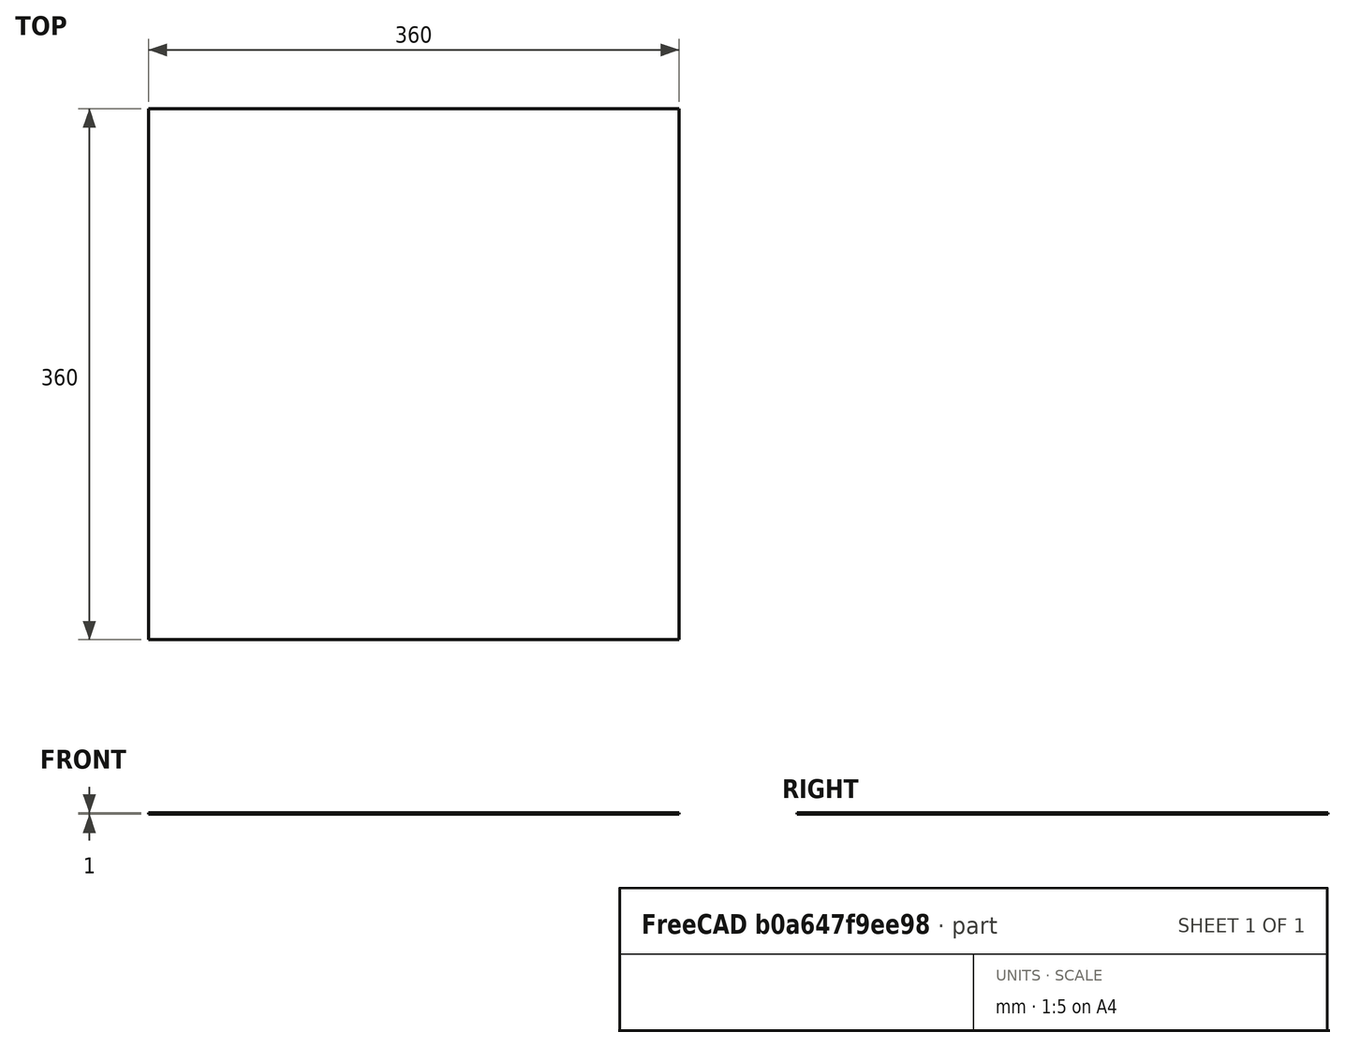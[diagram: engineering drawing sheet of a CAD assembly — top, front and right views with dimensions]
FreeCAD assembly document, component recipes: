
FREECAD ASSEMBLY — COMPONENT RECIPES ("parabolic_simulation")

This assembly document has 3 components, labeled P0..P2 below (a component is one placed body or linked part). 3 of them carry a construction recipe — the FreeCAD feature program that regenerates the part from scratch, quoted from this document or its linked companion documents; the rest are supplied as boundary geometry only. No exploded tour is included for this assembly.
COMPONENT P0 — recipe-attached ("TemOctagon", a linked part whose construction recipe lives in a companion FreeCAD document of the same project; that document's serialized recipe follows).
Construction recipe (the companion document, serialized — sketch geometry with constraints, then the solid features built on it; lengths are millimeters unless a unit is written):

FCSTD DOCUMENT  (FreeCAD 0.20R29603 (Git))
Label: tem_octagon
License: All rights reserved
LicenseURL: http://en.wikipedia.org/wiki/All_rights_reserved
objects: Part::Compound×18, Part::Cylinder×16, Part::Cut×10, Part::Feature×8, Part::FeaturePython×8, Part::Part2DObjectPython×2, Part::Extrusion×2
note: 64 computed .brp shape members not serialized (recipe doc carries the construction recipe); baked Part::Feature solids carry a one-line shape summary decoded from their .brp

FEATURE [Part::Part2DObjectPython] Wire  # Draft 2D object (typed FeaturePython)
  Area = 106458
  ChamferSize = 0
  Closed = true
  End = (74.24,179.24,-40)
  FilletRadius = 0
  Length = 1187.89
  MakeFace = true
  Placement = pos=(0,0,-40) rot=(0,0,1;0rad)
  Points = (9) [(74.24,179.24,-2.13163e-14),(179.24,74.24,0),(179.24,-74.24,0),(74.24,-179.24,0),(-74.24,-179.24,0),(-179.24,-74.24,0),(-179.24,74.24,0),(-74.24,179.24,0),(74.24,179.24,-2.13163e-14)]
  Start = (74.24,179.24,-40)
  Subdivisions = 0
FEATURE [Part::Extrusion] Extrude
  Base = -> Wire
  Dir = (0,0,1)
  DirMode = 2
  FaceMakerClass = Part::FaceMakerBullseye
  LengthFwd = 80
  LengthRev = 0
  Solid = false
  Symmetric = false
FEATURE [Part::Part2DObjectPython] Wire001  # Draft 2D object (typed FeaturePython)
  Area = 85639.1
  ChamferSize = 0
  Closed = true
  End = (66.59,160.76,-40)
  FilletRadius = 0
  Length = 1065.43
  MakeFace = true
  Placement = pos=(0,0,-40) rot=(0,0,1;0rad)
  Points = (9) [(66.59,160.76,0),(160.76,66.59,0),(160.76,-66.59,0),(66.59,-160.76,0),(-66.59,-160.76,0),(-160.76,-66.59,0),(-160.76,66.59,0),(-66.59,160.76,0),(66.59,160.76,0)]
  Start = (66.59,160.76,-40)
  Subdivisions = 0
FEATURE [Part::Extrusion] Extrude001
  Base = -> Wire001
  Dir = (0,0,1)
  DirMode = 2
  FaceMakerClass = Part::FaceMakerBullseye
  LengthFwd = 80
  LengthRev = 0
  Solid = false
  Symmetric = false
FEATURE [Part::Cut] Cut
  Base = -> Extrude
  Tool = -> Extrude001
FEATURE [Part::Feature] Solid  label="Hositrad_CF35-Blank"
  Placement = pos=(0,166.75,0) rot=(0,0,1;0rad)
  shape: bbox 70 x 12.7 x 70 mm, 58 faces (baked)
FEATURE [Part::Cylinder] Cylinder  label="Zylinder"
  Angle = 360
  AttacherType = Attacher::AttachEngine3D
  FirstAngle = 0
  Height = 20
  Placement = pos=(0,179.75,0) rot=(1,0,0;1.5708rad)
  Radius = 34.5
  SecondAngle = 0
FEATURE [Part::Cylinder] Cylinder001  label="Zylinder001"
  Angle = 360
  AttacherType = Attacher::AttachEngine3D
  FirstAngle = 0
  Height = 20
  Placement = pos=(0,179.75,0) rot=(1,0,0;1.5708rad)
  Radius = 22.25
  SecondAngle = 0
FEATURE [Part::Cylinder] Cylinder002  label="Zylinder002"
  Angle = 360
  AttacherType = Attacher::AttachEngine3D
  FirstAngle = 0
  Height = 20
  Placement = pos=(0,179.75,0) rot=(1,0,0;1.5708rad)
  Radius = 34.5
  SecondAngle = 0
FEATURE [Part::Compound] Compound
  Links = -> [Cylinder002]
  Placement = pos=(0,0,0) rot=(0,0,1;0.785398rad)
FEATURE [Part::Cylinder] Cylinder003  label="Zylinder003"
  Angle = 360
  AttacherType = Attacher::AttachEngine3D
  FirstAngle = 0
  Height = 20
  Placement = pos=(0,179.75,0) rot=(1,0,0;1.5708rad)
  Radius = 34.5
  SecondAngle = 0
FEATURE [Part::Compound] Compound001
  Links = -> [Cylinder003]
  Placement = pos=(0,0,0) rot=(0,0,1;1.5708rad)
FEATURE [Part::Cylinder] Cylinder004  label="Zylinder004"
  Angle = 360
  AttacherType = Attacher::AttachEngine3D
  FirstAngle = 0
  Height = 20
  Placement = pos=(0,179.75,0) rot=(1,0,0;1.5708rad)
  Radius = 34.5
  SecondAngle = 0
FEATURE [Part::Compound] Compound002
  Links = -> [Cylinder004]
  Placement = pos=(0,0,0) rot=(0,0,1;2.35619rad)
FEATURE [Part::Cylinder] Cylinder005  label="Zylinder005"
  Angle = 360
  AttacherType = Attacher::AttachEngine3D
  FirstAngle = 0
  Height = 20
  Placement = pos=(0,179.75,0) rot=(1,0,0;1.5708rad)
  Radius = 34.5
  SecondAngle = 0
FEATURE [Part::Compound] Compound003
  Links = -> [Cylinder005]
  Placement = pos=(0,0,0) rot=(0,0,1;3.14159rad)
FEATURE [Part::Cylinder] Cylinder006  label="Zylinder006"
  Angle = 360
  AttacherType = Attacher::AttachEngine3D
  FirstAngle = 0
  Height = 20
  Placement = pos=(0,179.75,0) rot=(1,0,0;1.5708rad)
  Radius = 34.5
  SecondAngle = 0
FEATURE [Part::Compound] Compound004
  Links = -> [Cylinder006]
  Placement = pos=(0,0,0) rot=(0,0,1;3.92699rad)
FEATURE [Part::Cylinder] Cylinder007  label="Zylinder007"
  Angle = 360
  AttacherType = Attacher::AttachEngine3D
  FirstAngle = 0
  Height = 20
  Placement = pos=(0,179.75,0) rot=(1,0,0;1.5708rad)
  Radius = 34.5
  SecondAngle = 0
FEATURE [Part::Compound] Compound005
  Links = -> [Cylinder007]
  Placement = pos=(0,0,0) rot=(0,0,1;4.71239rad)
FEATURE [Part::Cylinder] Cylinder008  label="Zylinder008"
  Angle = 360
  AttacherType = Attacher::AttachEngine3D
  FirstAngle = 0
  Height = 20
  Placement = pos=(0,179.75,0) rot=(1,0,0;1.5708rad)
  Radius = 34.5
  SecondAngle = 0
FEATURE [Part::Compound] Compound006
  Links = -> [Cylinder008]
  Placement = pos=(0,0,0) rot=(0,0,1;5.49779rad)
FEATURE [Part::Compound] Compound007
  Links = -> [Cylinder,Compound,Compound001,Compound002,Compound003,Compound004,Compound005,Compound006]
FEATURE [Part::Cut] Cut001
  Base = -> Cut
  Tool = -> Compound007
FEATURE [Part::Cut] Cut002
  Base = -> Solid
  Tool = -> Cylinder001
FEATURE [Part::FeaturePython] Tube  # WARN: FeaturePython — macro-defined, semantics opaque (R4)
  AttacherType = Attacher::AttachEngine3D
  Height = 6
  InnerRadius = 22.25
  OuterRadius = 34.5
  Placement = pos=(0,166.76,0) rot=(1,0,0;1.5708rad)
FEATURE [Part::Compound] Compound008
  Links = -> [Tube,Cut002]
FEATURE [Part::Cylinder] Cylinder009  label="Zylinder009"
  Angle = 360
  AttacherType = Attacher::AttachEngine3D
  FirstAngle = 0
  Height = 20
  Placement = pos=(0,179.75,0) rot=(1,0,0;1.5708rad)
  Radius = 22.25
  SecondAngle = 0
FEATURE [Part::Feature] Solid001  label="Hositrad_CF35-Blank001"
  Placement = pos=(0,166.75,0) rot=(0,0,1;0rad)
  shape: bbox 70 x 12.7 x 70 mm, 58 faces (baked)
FEATURE [Part::Cut] Cut003
  Base = -> Solid001
  Tool = -> Cylinder009
FEATURE [Part::FeaturePython] Tube001  # WARN: FeaturePython — macro-defined, semantics opaque (R4)
  AttacherType = Attacher::AttachEngine3D
  Height = 6
  InnerRadius = 22.25
  OuterRadius = 34.5
  Placement = pos=(0,166.76,0) rot=(1,0,0;1.5708rad)
FEATURE [Part::Compound] Compound009
  Links = -> [Tube001,Cut003]
  Placement = pos=(0,0,0) rot=(0,0,1;0.785398rad)
FEATURE [Part::Cylinder] Cylinder010  label="Zylinder010"
  Angle = 360
  AttacherType = Attacher::AttachEngine3D
  FirstAngle = 0
  Height = 20
  Placement = pos=(0,179.75,0) rot=(1,0,0;1.5708rad)
  Radius = 22.25
  SecondAngle = 0
FEATURE [Part::Feature] Solid002  label="Hositrad_CF35-Blank002"
  Placement = pos=(0,166.75,0) rot=(0,0,1;0rad)
  shape: bbox 70 x 12.7 x 70 mm, 58 faces (baked)
FEATURE [Part::Cut] Cut004
  Base = -> Solid002
  Tool = -> Cylinder010
FEATURE [Part::FeaturePython] Tube002  # WARN: FeaturePython — macro-defined, semantics opaque (R4)
  AttacherType = Attacher::AttachEngine3D
  Height = 6
  InnerRadius = 22.25
  OuterRadius = 34.5
  Placement = pos=(0,166.76,0) rot=(1,0,0;1.5708rad)
FEATURE [Part::Compound] Compound010
  Links = -> [Tube002,Cut004]
  Placement = pos=(0,0,0) rot=(0,0,1;1.5708rad)
FEATURE [Part::Cylinder] Cylinder011  label="Zylinder011"
  Angle = 360
  AttacherType = Attacher::AttachEngine3D
  FirstAngle = 0
  Height = 20
  Placement = pos=(0,179.75,0) rot=(1,0,0;1.5708rad)
  Radius = 22.25
  SecondAngle = 0
FEATURE [Part::Feature] Solid003  label="Hositrad_CF35-Blank003"
  Placement = pos=(0,166.75,0) rot=(0,0,1;0rad)
  shape: bbox 70 x 12.7 x 70 mm, 58 faces (baked)
FEATURE [Part::Cut] Cut005
  Base = -> Solid003
  Tool = -> Cylinder011
FEATURE [Part::FeaturePython] Tube003  # WARN: FeaturePython — macro-defined, semantics opaque (R4)
  AttacherType = Attacher::AttachEngine3D
  Height = 6
  InnerRadius = 22.25
  OuterRadius = 34.5
  Placement = pos=(0,166.76,0) rot=(1,0,0;1.5708rad)
FEATURE [Part::Compound] Compound011
  Links = -> [Tube003,Cut005]
  Placement = pos=(0,0,0) rot=(0,0,1;2.35619rad)
FEATURE [Part::Cylinder] Cylinder012  label="Zylinder012"
  Angle = 360
  AttacherType = Attacher::AttachEngine3D
  FirstAngle = 0
  Height = 20
  Placement = pos=(0,179.75,0) rot=(1,0,0;1.5708rad)
  Radius = 22.25
  SecondAngle = 0
FEATURE [Part::Feature] Solid004  label="Hositrad_CF35-Blank004"
  Placement = pos=(0,166.75,0) rot=(0,0,1;0rad)
  shape: bbox 70 x 12.7 x 70 mm, 58 faces (baked)
FEATURE [Part::Cut] Cut006
  Base = -> Solid004
  Tool = -> Cylinder012
FEATURE [Part::FeaturePython] Tube004  # WARN: FeaturePython — macro-defined, semantics opaque (R4)
  AttacherType = Attacher::AttachEngine3D
  Height = 6
  InnerRadius = 22.25
  OuterRadius = 34.5
  Placement = pos=(0,166.76,0) rot=(1,0,0;1.5708rad)
FEATURE [Part::Compound] Compound012
  Links = -> [Tube004,Cut006]
  Placement = pos=(0,0,0) rot=(0,0,1;3.14159rad)
FEATURE [Part::Cylinder] Cylinder013  label="Zylinder013"
  Angle = 360
  AttacherType = Attacher::AttachEngine3D
  FirstAngle = 0
  Height = 20
  Placement = pos=(0,179.75,0) rot=(1,0,0;1.5708rad)
  Radius = 22.25
  SecondAngle = 0
FEATURE [Part::Feature] Solid005  label="Hositrad_CF35-Blank005"
  Placement = pos=(0,166.75,0) rot=(0,0,1;0rad)
  shape: bbox 70 x 12.7 x 70 mm, 58 faces (baked)
FEATURE [Part::Cut] Cut007
  Base = -> Solid005
  Tool = -> Cylinder013
FEATURE [Part::FeaturePython] Tube005  # WARN: FeaturePython — macro-defined, semantics opaque (R4)
  AttacherType = Attacher::AttachEngine3D
  Height = 6
  InnerRadius = 22.25
  OuterRadius = 34.5
  Placement = pos=(0,166.76,0) rot=(1,0,0;1.5708rad)
FEATURE [Part::Compound] Compound013
  Links = -> [Tube005,Cut007]
  Placement = pos=(0,0,0) rot=(0,0,1;3.92699rad)
FEATURE [Part::Cylinder] Cylinder014  label="Zylinder014"
  Angle = 360
  AttacherType = Attacher::AttachEngine3D
  FirstAngle = 0
  Height = 20
  Placement = pos=(0,179.75,0) rot=(1,0,0;1.5708rad)
  Radius = 22.25
  SecondAngle = 0
FEATURE [Part::Feature] Solid006  label="Hositrad_CF35-Blank006"
  Placement = pos=(0,166.75,0) rot=(0,0,1;0rad)
  shape: bbox 70 x 12.7 x 70 mm, 58 faces (baked)
FEATURE [Part::Cut] Cut008
  Base = -> Solid006
  Tool = -> Cylinder014
FEATURE [Part::FeaturePython] Tube006  # WARN: FeaturePython — macro-defined, semantics opaque (R4)
  AttacherType = Attacher::AttachEngine3D
  Height = 6
  InnerRadius = 22.25
  OuterRadius = 34.5
  Placement = pos=(0,166.76,0) rot=(1,0,0;1.5708rad)
FEATURE [Part::Compound] Compound014
  Links = -> [Tube006,Cut008]
  Placement = pos=(0,0,0) rot=(0,0,1;4.71239rad)
FEATURE [Part::Cylinder] Cylinder015  label="Zylinder015"
  Angle = 360
  AttacherType = Attacher::AttachEngine3D
  FirstAngle = 0
  Height = 20
  Placement = pos=(0,179.75,0) rot=(1,0,0;1.5708rad)
  Radius = 22.25
  SecondAngle = 0
FEATURE [Part::Feature] Solid007  label="Hositrad_CF35-Blank007"
  Placement = pos=(0,166.75,0) rot=(0,0,1;0rad)
  shape: bbox 70 x 12.7 x 70 mm, 58 faces (baked)
FEATURE [Part::Cut] Cut009
  Base = -> Solid007
  Tool = -> Cylinder015
FEATURE [Part::FeaturePython] Tube007  # WARN: FeaturePython — macro-defined, semantics opaque (R4)
  AttacherType = Attacher::AttachEngine3D
  Height = 6
  InnerRadius = 22.25
  OuterRadius = 34.5
  Placement = pos=(0,166.76,0) rot=(1,0,0;1.5708rad)
FEATURE [Part::Compound] Compound015
  Links = -> [Tube007,Cut009]
  Placement = pos=(0,0,0) rot=(0,0,1;5.49779rad)
FEATURE [Part::Compound] Compound016
  Links = -> [Compound008,Compound009,Compound010,Compound011,Compound012,Compound013,Compound014,Compound015]
FEATURE [Part::Compound] Compound017
  Links = -> [Cut001,Compound016]
COMPONENT P1 — recipe-attached ("ParabolicMirrorWithScrewmount", a linked part whose construction recipe lives in a companion FreeCAD document of the same project; that document's serialized recipe follows).
Construction recipe (the companion document, serialized — sketch geometry with constraints, then the solid features built on it; lengths are millimeters unless a unit is written):

FCSTD DOCUMENT  (FreeCAD 0.19R24267 +99 (Git))
Label: parabolic_screwmount
License: All rights reserved
LicenseURL: http://en.wikipedia.org/wiki/All_rights_reserved
objects: Part::Cylinder×4, Part::Box×2, App::Link×1, Spreadsheet::Sheet×1, Part::Compound×1, Part::MultiFuse×1, Part::Cut×1
note: 9 computed .brp shape members not serialized (recipe doc carries the construction recipe); baked Part::Feature solids carry a one-line shape summary decoded from their .brp
EXTERNAL_REF file=parabolic_base.FCStd obj=Common
EXTERNAL_REF file=parabolic_base.FCStd obj=Spreadsheet

FEATURE [App::Link] Link  label="MirrorWithoutMount_Solid"
  LinkedObject = -> <external parabolic_base.FCStd>#Common
FEATURE [Spreadsheet::Sheet] Spreadsheet  label="ScrewMountParameters"
  cells = A1=Settings; E1=Importet properties (don't change here!); A2=Screw type; B2=M1; C2=Informative only (not updating below values); E2=Body offset; F2(body_offset)==<<parabolic_base>>#<<MirrorParameters>>.center_offset + <<parabolic_base>>#<<MirrorParameters>>.focal_length; G2=From parabolic_base: Offset of the body part with relation to Origin at the beamhole; A3=Through hole diameter; B3(mountscrew_through_dia)=1.2; C3=Close or medium fit diameter; E3=Body length; F3(body_length)==<<parabolic_base>>#<<MirrorParameters>>.tot_length; G3=From parabolic_base: Length of the body part; A4=Minimum material thickness; B4(min_material_thickness)=0.5; C4=Leave at least this amount of material if possible; E4=Body diameter; F4(body_width)==<<parabolic_base>>#<<MirrorParameters>>.max_width; G4=From parabolic_base: Diameter of body (max. width); A5=Screw head diameter; B5(screwhead_dia)=2; C5=Diameter of screw head; E5=Body height; F5(body_height)==<<parabolic_base>>#<<MirrorParameters>>.max_height; G5=From parabolic_base: Height of body (max body); A6=Screw head height max; B6(screwhead_height_max)==sqrt((body_width / 2) ^ 2 - (screwhead_dia / 2) ^ 2) - min_material_thickness; C6=Absolute maximum that leaves minimum material intact; A7=Screw head height real; B7(screwhead_height)=0.7; C7=Height of screw head; A8=Remaining material below screw head; B8(calculated_remaining_below_screwhead)==sqrt((body_width / 2) ^ 2 - (screwhead_dia / 2) ^ 2) - screwhead_height; C8=Remaining material below head of screw; A9=Remaining material on side of screw head; B9==(body_width - screwhead_dia) / 2; C9=Remaining material on both sides of the screw head; A10=Remaining material on side of screw; B10==(body_width - mountscrew_through_dia) / 2; C10=Remaining material on both sides of the screw
FEATURE [Part::Box] Box  label="CuttingToolThroughHole"
  AttacherType = Attacher::AttachEngine3D
  Height = 1.7
  Length = 4
  Placement = pos=(2.25,-0.6,0) rot=(0,0,1;0rad)
  Width = 1.2
  expr: Width = <<ScrewMountParameters>>.mountscrew_through_dia
  expr: Length = <<ScrewMountParameters>>.body_length - 2 * <<ScrewMountParameters>>.min_material_thickness - <<ScrewMountParameters>>.screwhead_dia
  expr: Height = <<ScrewMountParameters>>.body_height
  expr: .Placement.Base.y = -<<ScrewMountParameters>>.mountscrew_through_dia / 2
  expr: .Placement.Base.x = <<ScrewMountParameters>>.body_offset + <<ScrewMountParameters>>.min_material_thickness + <<ScrewMountParameters>>.screwhead_dia / 2
FEATURE [Part::Box] Box001  label="CuttingToolScrewHead"
  AttacherType = Attacher::AttachEngine3D
  Height = 0.942264
  Length = 4
  Placement = pos=(2.25,-1,1.24274) rot=(0,0,1;0rad)
  Width = 2
  expr: Width = <<ScrewMountParameters>>.screwhead_dia
  expr: Length = <<ScrewMountParameters>>.body_length - 2 * <<ScrewMountParameters>>.min_material_thickness - <<ScrewMountParameters>>.screwhead_dia
  expr: Height = <<ScrewMountParameters>>.body_width / 2 - <<ScrewMountParameters>>.calculated_remaining_below_screwhead
  expr: .Placement.Base.z = <<ScrewMountParameters>>.calculated_remaining_below_screwhead
  expr: .Placement.Base.y = -<<ScrewMountParameters>>.screwhead_dia / 2
  expr: .Placement.Base.x = <<ScrewMountParameters>>.body_offset + <<ScrewMountParameters>>.min_material_thickness + <<ScrewMountParameters>>.screwhead_dia / 2
FEATURE [Part::Compound] Compound
  Links = -> [Link]
FEATURE [Part::Cylinder] Cylinder  label="HeadFront"
  Angle = 360
  AttacherType = Attacher::AttachEngine3D
  Height = 10
  Placement = pos=(2.25,0,1.24274) rot=(0,0,1;0rad)
  Radius = 1
  expr: .Placement.Base.x = <<ScrewMountParameters>>.body_offset + <<ScrewMountParameters>>.min_material_thickness + <<ScrewMountParameters>>.screwhead_dia / 2
  expr: .Placement.Base.z = <<ScrewMountParameters>>.calculated_remaining_below_screwhead
  expr: Radius = <<ScrewMountParameters>>.screwhead_dia / 2
FEATURE [Part::Cylinder] Cylinder001  label="HeadBack"
  Angle = 360
  AttacherType = Attacher::AttachEngine3D
  Height = 10
  Placement = pos=(6.25,0,1.24274) rot=(0,0,1;0rad)
  Radius = 1
  expr: Radius = <<ScrewMountParameters>>.screwhead_dia / 2
  expr: .Placement.Base.z = <<ScrewMountParameters>>.calculated_remaining_below_screwhead
  expr: .Placement.Base.x = <<ScrewMountParameters>>.body_offset + <<ScrewMountParameters>>.min_material_thickness + <<ScrewMountParameters>>.screwhead_dia / 2 + <<ScrewMountParameters>>.body_length - 2 * <<ScrewMountParameters>>.min_material_thickness - <<ScrewMountParameters>>.screwhead_dia
FEATURE [Part::Cylinder] Cylinder002  label="ScrewThroughFront"
  Angle = 360
  AttacherType = Attacher::AttachEngine3D
  Height = 10
  Placement = pos=(2.25,0,0) rot=(0,0,1;0rad)
  Radius = 0.6
  expr: .Placement.Base.y = 0
  expr: Radius = <<ScrewMountParameters>>.mountscrew_through_dia / 2
  expr: .Placement.Base.x = <<ScrewMountParameters>>.body_offset + <<ScrewMountParameters>>.min_material_thickness + <<ScrewMountParameters>>.screwhead_dia / 2
FEATURE [Part::Cylinder] Cylinder003  label="ScrewThroughBack"
  Angle = 360
  AttacherType = Attacher::AttachEngine3D
  Height = 10
  Placement = pos=(6.25,0,0) rot=(0,0,1;0rad)
  Radius = 0.6
  expr: .Placement.Base.x = <<ScrewMountParameters>>.body_offset + <<ScrewMountParameters>>.min_material_thickness + <<ScrewMountParameters>>.screwhead_dia / 2 + <<ScrewMountParameters>>.body_length - 2 * <<ScrewMountParameters>>.min_material_thickness - <<ScrewMountParameters>>.screwhead_dia
  expr: Radius = <<ScrewMountParameters>>.mountscrew_through_dia / 2
FEATURE [Part::MultiFuse] Fusion  label="CuttingTools"
  Shapes = -> [Box001,Box,Cylinder,Cylinder001,Cylinder002,Cylinder003]
FEATURE [Part::Cut] Cut  label="ParabolicMirrorWithScrewmount"
  Base = -> Compound
  Tool = -> Fusion
COMPONENT P2 — recipe-attached ("TemHolder", a linked part whose construction recipe lives in a companion FreeCAD document of the same project; that document's serialized recipe follows).
Construction recipe (the companion document, serialized — sketch geometry with constraints, then the solid features built on it; lengths are millimeters unless a unit is written):

FCSTD DOCUMENT  (FreeCAD 0.21R33675 (Git))
Label: temholder2
License: All rights reserved
LicenseURL: http://en.wikipedia.org/wiki/All_rights_reserved
objects: TechDraw::DrawViewDimension×22, Part::Cylinder×10, TechDraw::DrawProjGroupItem×10, Part::Cut×8, Part::Box×7, Part::MultiFuse×6, TechDraw::DrawSVGTemplate×2, TechDraw::DrawProjGroup×2, TechDraw::DrawPage×2, Part::MultiCommon×1
note: 32 computed .brp shape members not serialized (recipe doc carries the construction recipe); baked Part::Feature solids carry a one-line shape summary decoded from their .brp

FEATURE [Part::Cylinder] Cylinder  label="Zylinder"
  Angle = 360
  AttacherType = Attacher::AttachEngine3D
  FirstAngle = 0
  Height = 21.5
  Placement = pos=(0,0,-0.5) rot=(0,0,1;0rad)
  Radius = 2.2
  SecondAngle = 0
FEATURE [Part::Cylinder] Cylinder001  label="Zylinder001"
  Angle = 360
  AttacherType = Attacher::AttachEngine3D
  FirstAngle = 0
  Height = 18
  Placement = pos=(0,0,5) rot=(0,0,1;0rad)
  Radius = 2.5
  SecondAngle = 0
FEATURE [Part::Cylinder] Cylinder002  label="Zylinder002"
  Angle = 360
  AttacherType = Attacher::AttachEngine3D
  FirstAngle = 0
  Height = 6.2
  Placement = pos=(-3.25,0,2.95) rot=(0,1,0;1.5708rad)
  Radius = 0.75
  SecondAngle = 0
FEATURE [Part::MultiFuse] Fusion
  Shapes = -> [Cylinder,Cylinder001]
FEATURE [Part::Cut] Cut
  Base = -> Fusion
  Tool = -> Cylinder002
FEATURE [Part::Box] Box  label="Würfel"
  AttacherType = Attacher::AttachEngine3D
  Height = 27.9
  Length = 2
  Placement = pos=(-1,-5,21) rot=(0,0,1;0rad)
  Width = 10
FEATURE [Part::Cylinder] Cylinder003  label="BeamHole"
  Angle = 360
  AttacherType = Attacher::AttachEngine3D
  FirstAngle = 0
  Height = 2
  Placement = pos=(-1,0,35.2) rot=(0,1,0;1.5708rad)
  Radius = 1.1
  SecondAngle = 0
FEATURE [Part::Cylinder] Cylinder004  label="Zylinder004"
  Angle = 360
  AttacherType = Attacher::AttachEngine3D
  FirstAngle = 0
  Height = 27.4
  Placement = pos=(0,0,21.5) rot=(0,0,1;0rad)
  Radius = 3
  SecondAngle = 0
FEATURE [Part::MultiCommon] Common
  Shapes = -> [Cylinder004,Box]
FEATURE [Part::Cut] Cut001
  Base = -> Common
  Tool = -> Cylinder003
FEATURE [Part::Cylinder] Cylinder005  label="Zylinder005"
  Angle = 360
  AttacherType = Attacher::AttachEngine3D
  FirstAngle = 0
  Height = 5.5
  Placement = pos=(0,0,-0.5) rot=(0,0,1;0rad)
  Radius = 1
  SecondAngle = 0
FEATURE [Part::Cut] Cut002
  Base = -> Cut
  Tool = -> Cylinder005
FEATURE [Part::Cylinder] Cylinder006  label="ProbeHole"
  Angle = 360
  AttacherType = Attacher::AttachEngine3D
  FirstAngle = 0
  Height = 20
  Placement = pos=(-4,0,35.2) rot=(0,1,0;1.5708rad)
  Radius = 1.695
  SecondAngle = 0
FEATURE [Part::Cut] Cut003
  Base = -> Cut001
  Tool = -> Cylinder006
FEATURE [Part::Box] Box001  label="Würfel001"
  AttacherType = Attacher::AttachEngine3D
  Height = 27
  Length = 10
  Placement = pos=(1,-2.57,21) rot=(0,0,1;0rad)
  Width = 5.5
FEATURE [Part::Cut] Cut004
  Base = -> Cut003
  Tool = -> Box001
FEATURE [Part::MultiFuse] Fusion001
  Shapes = -> [Cut002,Cut004]
FEATURE [Part::Box] Box002  label="Würfel002"
  AttacherType = Attacher::AttachEngine3D
  Height = 1.5
  Length = 1
  Placement = pos=(-0.5,-3.2,21.5) rot=(0,0,1;0rad)
  Width = 6.4
FEATURE [Part::Box] Box003  label="Würfel003"
  AttacherType = Attacher::AttachEngine3D
  Height = 26
  Length = 10
  Placement = pos=(0.5,-2.19,23) rot=(0,0,1;0rad)
  Width = 4.37
FEATURE [Part::Box] Box004  label="Würfel004"
  AttacherType = Attacher::AttachEngine3D
  Height = 26
  Length = 10
  Placement = pos=(-10.5,-2.19,23) rot=(0,0,1;0rad)
  Width = 4.37
FEATURE [Part::MultiFuse] Fusion002  label="MirrorGrooves"
  Shapes = -> [Box004,Box003]
FEATURE [Part::Cut] Cut005
  Base = -> Fusion001
  Tool = -> Fusion002
FEATURE [Part::Cylinder] Cylinder007  label="M1_6__Thread1"
  Angle = 360
  AttacherType = Attacher::AttachEngine3D
  FirstAngle = 0
  Height = 50
  Placement = pos=(-4,0,31.405) rot=(0,1,0;1.5708rad)
  Radius = 0.59
  SecondAngle = 0
FEATURE [Part::Cylinder] Cylinder008  label="M1_6__Thread2"
  Angle = 360
  AttacherType = Attacher::AttachEngine3D
  FirstAngle = 0
  Height = 50
  Placement = pos=(-4,0,29.41) rot=(0,1,0;1.5708rad)
  Radius = 0.59
  SecondAngle = 0
FEATURE [Part::Box] Box005  label="Würfel005"
  AttacherType = Attacher::AttachEngine3D
  Height = 12
  Length = 10
  Placement = pos=(0.25,-2.19,36.77) rot=(0,0,1;0rad)
  Width = 4.37
FEATURE [Part::Box] Box006  label="Würfel006"
  AttacherType = Attacher::AttachEngine3D
  Height = 12
  Length = 10
  Placement = pos=(-10.25,-2.19,36.77) rot=(0,0,1;0rad)
  Width = 4.37
FEATURE [Part::MultiFuse] Fusion004
  Placement = pos=(0,0,1) rot=(0,0,1;0rad)
  Shapes = -> [Box005,Box006]
FEATURE [TechDraw::DrawSVGTemplate] Template
  EditableTexts = Designed_by_Name=Thomas Spielauer; Drawing_number=001; FC-Date=2023-05-22; FC-SC=2:1; FC-SH=2/2; FC-Title=TEM Mirror Holder; Subtitle=Version 2023-05-22
  Height = 210
  Orientation = 1
  Width = 297
FEATURE [TechDraw::DrawSVGTemplate] Template001
  EditableTexts = Designed_by_Name=Thomas Spielauer; Drawing_number=001; FC-Date=2023-05-22; FC-SC=3:2; FC-SH=2/2; FC-Title=TEM Mirror Holder; Subtitle=Version 2023-05-22
  Height = 210
  Orientation = 1
  Width = 297
FEATURE [Part::Cylinder] Cylinder009  label="M1_6__Thread3"
  Angle = 360
  AttacherType = Attacher::AttachEngine3D
  FirstAngle = 0
  Height = 50
  Placement = pos=(-4,0,27.41) rot=(0,1,0;1.5708rad)
  Radius = 0.59
  SecondAngle = 0
FEATURE [Part::MultiFuse] Fusion003  label="MirrorMountingHoles"
  Shapes = -> [Cylinder007,Cylinder008,Cylinder009]
FEATURE [Part::Cut] Cut006
  Base = -> Cut005
  Tool = -> Fusion003
FEATURE [Part::Cut] Cut007
  Base = -> Cut006
  Tool = -> Fusion004
FEATURE [Part::MultiFuse] Fusion005
  Shapes = -> [Cut007,Box002]
FEATURE [TechDraw::DrawProjGroupItem] ProjItem  label="Front"
  CoarseView = false
  Direction = (1,0,0)
  Focus = 100
  HardHidden = false
  IsoCount = 0
  IsoHidden = false
  IsoVisible = false
  LockPosition = true
  Perspective = false
  Rotation = 0
  RotationVector = (0,1,0)
  Scale = 2
  ScaleType = 2
  ScrubCount = 0
  SeamHidden = false
  SeamVisible = true
  SmoothHidden = false
  SmoothVisible = true
  Source = -> [Fusion005]
  Type = 0
  X = 0
  XDirection = (0,-2e-16,-1)
  Y = 0
FEATURE [TechDraw::DrawProjGroupItem] ProjItem001  label="Left"
  CoarseView = false
  Direction = (1e-16,2e-16,1)
  Focus = 100
  HardHidden = false
  IsoCount = 0
  IsoHidden = false
  IsoVisible = false
  LockPosition = false
  Perspective = false
  Rotation = 0
  RotationVector = (1,0,0)
  Scale = 2
  ScaleType = 2
  ScrubCount = 0
  SeamHidden = false
  SeamVisible = true
  SmoothHidden = false
  SmoothVisible = true
  Source = -> [Fusion005]
  Type = 1
  X = 54.4
  XDirection = (1,0,-1e-16)
  Y = 0
FEATURE [TechDraw::DrawProjGroupItem] ProjItem003  label="Right"
  CoarseView = false
  Direction = (1e-16,-2e-16,-1)
  Focus = 100
  HardHidden = false
  IsoCount = 0
  IsoHidden = false
  IsoVisible = false
  LockPosition = false
  Perspective = false
  Rotation = 0
  RotationVector = (1,0,0)
  Scale = 2
  ScaleType = 2
  ScrubCount = 0
  SeamHidden = false
  SeamVisible = true
  SmoothHidden = false
  SmoothVisible = true
  Source = -> [Fusion005]
  Type = 2
  X = -54.4
  XDirection = (-1,0,-1e-16)
  Y = 0
FEATURE [TechDraw::DrawProjGroupItem] ProjItem004  label="Bottom"
  CoarseView = false
  Direction = (0,-1,2e-16)
  Focus = 100
  HardHidden = false
  IsoCount = 0
  IsoHidden = false
  IsoVisible = false
  LockPosition = false
  Perspective = false
  Rotation = 0
  RotationVector = (1,0,0)
  ScaleType = 2
  ScrubCount = 0
  SeamHidden = false
  SeamVisible = true
  SmoothHidden = false
  SmoothVisible = true
  Source = -> [Fusion005]
  Type = 5
  X = 0
  XDirection = (0,-2e-16,-1)
  Y = 41.4
FEATURE [TechDraw::DrawProjGroup] ProjGroup
  Anchor = -> ProjItem
  AutoDistribute = true
  LockPosition = false
  ProjectionType = 0
  Rotation = 0
  Scale = 2
  ScaleType = 1
  Source = -> [Fusion005]
  Views = -> [ProjItem,ProjItem001,ProjItem003,ProjItem004]
  X = 148.5
  Y = 105
  spacingX = 0
  spacingY = 30
FEATURE [TechDraw::DrawViewDimension] Dimension
  AngleOverride = false
  Arbitrary = false
  ArbitraryTolerances = false
  EqualTolerance = true
  ExtensionAngle = 0
  FormatSpec = %.2w
  FormatSpecOverTolerance = %+.2w
  FormatSpecUnderTolerance = %+.2w
  Inverted = false
  LineAngle = 0
  LockPosition = false
  MeasureType = 1
  OverTolerance = 0
  References2D = -> [ProjItem004]
  Rotation = 0
  ScaleType = 0
  TheoreticalExact = false
  Type = 0
  UnderTolerance = 0
  X = -0.570385
  Y = 36.7256
FEATURE [TechDraw::DrawViewDimension] Dimension001
  AngleOverride = false
  Arbitrary = false
  ArbitraryTolerances = false
  EqualTolerance = true
  ExtensionAngle = 0
  FormatSpec = %.2w
  FormatSpecOverTolerance = %+.2w
  FormatSpecUnderTolerance = %+.2w
  Inverted = false
  LineAngle = 0
  LockPosition = false
  MeasureType = 1
  OverTolerance = 0
  References2D = -> [ProjItem004]
  Rotation = 0
  ScaleType = 0
  TheoreticalExact = false
  Type = 0
  UnderTolerance = 0
  X = 43.2488
  Y = 27.3992
FEATURE [TechDraw::DrawViewDimension] Dimension002
  AngleOverride = false
  Arbitrary = false
  ArbitraryTolerances = false
  EqualTolerance = true
  ExtensionAngle = 0
  FormatSpec = %.2w
  FormatSpecOverTolerance = %+.2w
  FormatSpecUnderTolerance = %+.2w
  Inverted = false
  LineAngle = 0
  LockPosition = false
  MeasureType = 1
  OverTolerance = 0
  References2D = -> [ProjItem004]
  Rotation = 0
  ScaleType = 0
  TheoreticalExact = false
  Type = 0
  UnderTolerance = 0
  X = 20.4028
  Y = 27.4177
FEATURE [TechDraw::DrawViewDimension] Dimension003
  AngleOverride = false
  Arbitrary = false
  ArbitraryTolerances = false
  EqualTolerance = true
  ExtensionAngle = 0
  FormatSpec = %.2w
  FormatSpecOverTolerance = %+.2w
  FormatSpecUnderTolerance = %+.2w
  Inverted = false
  LineAngle = 0
  LockPosition = false
  MeasureType = 1
  OverTolerance = 0
  References2D = -> [ProjItem004]
  Rotation = 0
  ScaleType = 0
  TheoreticalExact = false
  Type = 0
  UnderTolerance = 0
  X = -20.5047
  Y = 16.0274
FEATURE [TechDraw::DrawViewDimension] Dimension004
  AngleOverride = false
  Arbitrary = false
  ArbitraryTolerances = false
  EqualTolerance = true
  ExtensionAngle = 0
  FormatSpec = %.2w
  FormatSpecOverTolerance = %+.2w
  FormatSpecUnderTolerance = %+.2w
  Inverted = false
  LineAngle = 0
  LockPosition = false
  MeasureType = 1
  OverTolerance = 0
  References2D = -> [ProjItem004]
  Rotation = 0
  ScaleType = 0
  TheoreticalExact = false
  Type = 0
  UnderTolerance = 0
  X = 8.18137
  Y = 19.112
FEATURE [TechDraw::DrawViewDimension] Dimension005
  AngleOverride = false
  Arbitrary = false
  ArbitraryTolerances = false
  EqualTolerance = true
  ExtensionAngle = 0
  FormatSpec = %.2w
  FormatSpecOverTolerance = %+.2w
  FormatSpecUnderTolerance = %+.2w
  Inverted = false
  LineAngle = 0
  LockPosition = false
  MeasureType = 1
  OverTolerance = 0
  References2D = -> [ProjItem004]
  Rotation = 0
  ScaleType = 0
  TheoreticalExact = false
  Type = 0
  UnderTolerance = 0
  X = 68.2961
  Y = 3.13583
FEATURE [TechDraw::DrawViewDimension] Dimension006
  AngleOverride = false
  Arbitrary = false
  ArbitraryTolerances = false
  EqualTolerance = true
  ExtensionAngle = 0
  FormatSpec = %.2w
  FormatSpecOverTolerance = %+.2w
  FormatSpecUnderTolerance = %+.2w
  Inverted = false
  LineAngle = 0
  LockPosition = false
  MeasureType = 1
  OverTolerance = 0
  References2D = -> [ProjItem004]
  Rotation = 0
  ScaleType = 0
  TheoreticalExact = false
  Type = 0
  UnderTolerance = 0
  X = 78.1774
  Y = 10.4092
FEATURE [TechDraw::DrawViewDimension] Dimension007
  AngleOverride = false
  Arbitrary = false
  ArbitraryTolerances = false
  EqualTolerance = true
  ExtensionAngle = 0
  FormatSpec = %.2w
  FormatSpecOverTolerance = %+.2w
  FormatSpecUnderTolerance = %+.2w
  Inverted = false
  LineAngle = 0
  LockPosition = false
  MeasureType = 1
  OverTolerance = 0
  References2D = -> [ProjItem004]
  Rotation = 0
  ScaleType = 0
  TheoreticalExact = false
  Type = 0
  UnderTolerance = 0
  X = -59.0159
  Y = 3.08043
FEATURE [TechDraw::DrawViewDimension] Dimension008
  AngleOverride = false
  Arbitrary = false
  ArbitraryTolerances = false
  EqualTolerance = true
  ExtensionAngle = 0
  FormatSpec = %.2w
  FormatSpecOverTolerance = %+.2w
  FormatSpecUnderTolerance = %+.2w
  Inverted = false
  LineAngle = 0
  LockPosition = false
  MeasureType = 1
  OverTolerance = 0
  References2D = -> [ProjItem004]
  Rotation = 0
  ScaleType = 0
  TheoreticalExact = false
  Type = 0
  UnderTolerance = 0
  X = 17.8117
  Y = -5.66689
FEATURE [TechDraw::DrawViewDimension] Dimension010
  AngleOverride = false
  Arbitrary = false
  ArbitraryTolerances = false
  EqualTolerance = true
  ExtensionAngle = 0
  FormatSpec = %.2w
  FormatSpecOverTolerance = %+.2w
  FormatSpecUnderTolerance = %+.2w
  Inverted = false
  LineAngle = 0
  LockPosition = false
  MeasureType = 1
  OverTolerance = 0
  References2D = -> [ProjItem]
  Rotation = 0
  ScaleType = 0
  TheoreticalExact = false
  Type = 0
  UnderTolerance = 0
  X = -80.5776
  Y = 1.58527
FEATURE [TechDraw::DrawViewDimension] Dimension011
  AngleOverride = false
  Arbitrary = false
  ArbitraryTolerances = false
  EqualTolerance = true
  ExtensionAngle = 0
  FormatSpec = %.2w
  FormatSpecOverTolerance = %+.2w
  FormatSpecUnderTolerance = %+.2w
  Inverted = false
  LineAngle = 0
  LockPosition = false
  MeasureType = 1
  OverTolerance = 0
  References2D = -> [ProjItem]
  Rotation = 0
  ScaleType = 0
  TheoreticalExact = false
  Type = 0
  UnderTolerance = 0
  X = -69.6018
  Y = 1.50597
FEATURE [TechDraw::DrawViewDimension] Dimension012
  AngleOverride = false
  Arbitrary = false
  ArbitraryTolerances = false
  EqualTolerance = true
  ExtensionAngle = 0
  FormatSpec = %.2w
  FormatSpecOverTolerance = %+.2w
  FormatSpecUnderTolerance = %+.2w
  Inverted = false
  LineAngle = 0
  LockPosition = false
  MeasureType = 1
  OverTolerance = 0
  References2D = -> [ProjItem]
  Rotation = 0
  ScaleType = 0
  TheoreticalExact = false
  Type = 0
  UnderTolerance = 0
  X = 80.5725
  Y = 4.77787
FEATURE [TechDraw::DrawViewDimension] Dimension013
  AngleOverride = false
  Arbitrary = false
  ArbitraryTolerances = false
  EqualTolerance = true
  ExtensionAngle = 0
  FormatSpec = %.2w
  FormatSpecOverTolerance = %+.2w
  FormatSpecUnderTolerance = %+.2w
  Inverted = false
  LineAngle = 0
  LockPosition = false
  MeasureType = 1
  OverTolerance = 0
  References2D = -> [ProjItem]
  Rotation = 0
  ScaleType = 0
  TheoreticalExact = false
  Type = 0
  UnderTolerance = 0
  X = 58.3431
  Y = 1.78358
FEATURE [TechDraw::DrawViewDimension] Dimension014
  AngleOverride = false
  Arbitrary = false
  ArbitraryTolerances = false
  EqualTolerance = true
  ExtensionAngle = 0
  FormatSpec = %.2w
  FormatSpecOverTolerance = %+.2w
  FormatSpecUnderTolerance = %+.2w
  Inverted = false
  LineAngle = 0
  LockPosition = false
  MeasureType = 1
  OverTolerance = 0
  References2D = -> [ProjItem]
  Rotation = 0
  ScaleType = 0
  TheoreticalExact = false
  Type = 0
  UnderTolerance = 0
  X = 69.2835
  Y = 2.85821
FEATURE [TechDraw::DrawViewDimension] Dimension015
  AngleOverride = false
  Arbitrary = false
  ArbitraryTolerances = false
  EqualTolerance = true
  ExtensionAngle = 0
  FormatSpec = ⌀%.2w
  FormatSpecOverTolerance = %+.2w
  FormatSpecUnderTolerance = %+.2w
  Inverted = false
  LineAngle = 0
  LockPosition = false
  MeasureType = 1
  OverTolerance = 0
  References2D = -> [ProjItem]
  Rotation = 0
  ScaleType = 0
  TheoreticalExact = false
  Type = 5
  UnderTolerance = 0
  X = -17.8818
  Y = -30.5126
FEATURE [TechDraw::DrawViewDimension] Dimension016
  AngleOverride = false
  Arbitrary = false
  ArbitraryTolerances = false
  EqualTolerance = true
  ExtensionAngle = 0
  FormatSpec = ⌀%.2w
  FormatSpecOverTolerance = %+.2w
  FormatSpecUnderTolerance = %+.2w
  Inverted = false
  LineAngle = 0
  LockPosition = false
  MeasureType = 1
  OverTolerance = 0
  References2D = -> [ProjItem]
  Rotation = 0
  ScaleType = 0
  TheoreticalExact = false
  Type = 5
  UnderTolerance = 0
  X = -6.5506
  Y = -20.9661
FEATURE [TechDraw::DrawViewDimension] Dimension017
  AngleOverride = false
  Arbitrary = false
  ArbitraryTolerances = false
  EqualTolerance = true
  ExtensionAngle = 0
  FormatSpec = ⌀%.2w
  FormatSpecOverTolerance = %+.2w
  FormatSpecUnderTolerance = %+.2w
  Inverted = false
  LineAngle = 0
  LockPosition = false
  MeasureType = 1
  OverTolerance = 0
  References2D = -> [ProjItem]
  Rotation = 0
  ScaleType = 0
  TheoreticalExact = false
  Type = 5
  UnderTolerance = 0
  X = 0
  Y = -20.3856
FEATURE [TechDraw::DrawViewDimension] Dimension018
  AngleOverride = false
  Arbitrary = false
  ArbitraryTolerances = false
  EqualTolerance = true
  ExtensionAngle = 0
  FormatSpec = %.2w
  FormatSpecOverTolerance = %+.2w
  FormatSpecUnderTolerance = %+.2w
  Inverted = false
  LineAngle = 0
  LockPosition = false
  MeasureType = 1
  OverTolerance = 0
  References2D = -> [ProjItem]
  Rotation = 0
  ScaleType = 0
  TheoreticalExact = false
  Type = 0
  UnderTolerance = 0
  X = 37.2627
  Y = -7.40421
FEATURE [TechDraw::DrawViewDimension] Dimension019
  AngleOverride = false
  Arbitrary = false
  ArbitraryTolerances = false
  EqualTolerance = true
  ExtensionAngle = 0
  FormatSpec = %.2w
  FormatSpecOverTolerance = %+.2w
  FormatSpecUnderTolerance = %+.2w
  Inverted = false
  LineAngle = 0
  LockPosition = false
  MeasureType = 1
  OverTolerance = 0
  References2D = -> [ProjItem001]
  Rotation = 0
  ScaleType = 0
  TheoreticalExact = false
  Type = 0
  UnderTolerance = 0
  X = 14.265
  Y = 2.24769
FEATURE [TechDraw::DrawViewDimension] Dimension020
  AngleOverride = false
  Arbitrary = false
  ArbitraryTolerances = false
  EqualTolerance = true
  ExtensionAngle = 0
  FormatSpec = ⌀%.2w
  FormatSpecOverTolerance = %+.2w
  FormatSpecUnderTolerance = %+.2w
  Inverted = false
  LineAngle = 0
  LockPosition = false
  MeasureType = 1
  OverTolerance = 0
  References2D = -> [ProjItem001]
  Rotation = 0
  ScaleType = 0
  TheoreticalExact = false
  Type = 5
  UnderTolerance = 0
  X = -8.46963
  Y = -24.8974
FEATURE [TechDraw::DrawViewDimension] Dimension021
  AngleOverride = false
  Arbitrary = false
  ArbitraryTolerances = false
  EqualTolerance = true
  ExtensionAngle = 0
  FormatSpec = %.2w
  FormatSpecOverTolerance = %+.2w
  FormatSpecUnderTolerance = %+.2w
  Inverted = false
  LineAngle = 0
  LockPosition = false
  MeasureType = 1
  OverTolerance = 0
  References2D = -> [ProjItem003]
  Rotation = 0
  ScaleType = 0
  TheoreticalExact = false
  Type = 0
  UnderTolerance = 0
  X = 0
  Y = 15.8224
FEATURE [TechDraw::DrawViewDimension] Dimension022
  AngleOverride = false
  Arbitrary = false
  ArbitraryTolerances = false
  EqualTolerance = true
  ExtensionAngle = 0
  FormatSpec = %.2w
  FormatSpecOverTolerance = %+.2w
  FormatSpecUnderTolerance = %+.2w
  Inverted = false
  LineAngle = 0
  LockPosition = false
  MeasureType = 1
  OverTolerance = 0
  References2D = -> [ProjItem003]
  Rotation = 0
  ScaleType = 0
  TheoreticalExact = false
  Type = 0
  UnderTolerance = 0
  X = -0.516427
  Y = -17.6903
FEATURE [TechDraw::DrawPage] Page
  KeepUpdated = true
  NextBalloonIndex = 1
  ProjectionType = 0
  Template = -> Template
  Views = -> [ProjGroup,Dimension,Dimension001,Dimension002,Dimension003,Dimension004,Dimension005,Dimension006,Dimension007,Dimension008,Dimension010,Dimension011,Dimension012,Dimension013,Dimension014,Dimension015,Dimension016,Dimension017,Dimension018,Dimension019,Dimension020,Dimension021,Dimension022]
FEATURE [TechDraw::DrawProjGroupItem] ProjItem005  label="Front001"
  CoarseView = false
  Direction = (0.582,-0.433,-0.688)
  Focus = 100
  HardHidden = false
  IsoCount = 0
  IsoHidden = false
  IsoVisible = false
  LockPosition = true
  Perspective = false
  Rotation = 0
  RotationVector = (-0.012,0.841,-0.54)
  Scale = 1.5
  ScaleType = 2
  ScrubCount = 0
  SeamHidden = false
  SeamVisible = true
  SmoothHidden = false
  SmoothVisible = true
  Source = -> [Fusion005]
  Type = 0
  X = 0
  XDirection = (-0.012,0.841,-0.54)
  Y = 0
FEATURE [TechDraw::DrawProjGroupItem] ProjItem006  label="FrontBottomRight"
  CoarseView = false
  Direction = (-0.140356,0.0494879,-0.988863)
  Focus = 100
  HardHidden = false
  IsoCount = 0
  IsoHidden = false
  IsoVisible = false
  LockPosition = false
  Perspective = false
  Rotation = 0
  RotationVector = (1,0,0)
  Scale = 1.5
  ScaleType = 2
  ScrubCount = 0
  SeamHidden = false
  SeamVisible = true
  SmoothHidden = false
  SmoothVisible = true
  Source = -> [Fusion005]
  Type = 9
  X = -51.338
  XDirection = (-0.420275,0.901329,0.10476)
  Y = 48.7411
FEATURE [TechDraw::DrawProjGroupItem] ProjItem007  label="FrontBottomLeft"
  CoarseView = false
  Direction = (-0.126236,-0.922281,-0.365326)
  Focus = 100
  HardHidden = false
  IsoCount = 0
  IsoHidden = false
  IsoVisible = false
  LockPosition = false
  Perspective = false
  Rotation = 0
  RotationVector = (1,0,0)
  Scale = 1.5
  ScaleType = 2
  ScrubCount = 0
  SeamHidden = false
  SeamVisible = true
  SmoothHidden = false
  SmoothVisible = true
  Source = -> [Fusion005]
  Type = 8
  X = 57.198
  XDirection = (0.40298,0.288839,-0.868435)
  Y = 48.7411
FEATURE [TechDraw::DrawProjGroupItem] ProjItem008  label="Left001"
  CoarseView = false
  Direction = (0.012229,-0.841576,0.54)
  Focus = 100
  HardHidden = false
  IsoCount = 0
  IsoHidden = false
  IsoVisible = false
  LockPosition = false
  Perspective = false
  Rotation = 0
  RotationVector = (1,0,0)
  Scale = 1.5
  ScaleType = 2
  ScrubCount = 0
  SeamHidden = false
  SeamVisible = true
  SmoothHidden = false
  SmoothVisible = true
  Source = -> [Fusion005]
  Type = 1
  X = 57.198
  XDirection = (0.582129,-0.433096,-0.688152)
  Y = 0
FEATURE [TechDraw::DrawProjGroupItem] ProjItem009  label="Right001"
  CoarseView = false
  Direction = (-0.012229,0.841576,-0.54)
  Focus = 100
  HardHidden = false
  IsoCount = 0
  IsoHidden = false
  IsoVisible = false
  LockPosition = false
  Perspective = false
  Rotation = 0
  RotationVector = (1,0,0)
  Scale = 1.5
  ScaleType = 2
  ScrubCount = 0
  SeamHidden = false
  SeamVisible = true
  SmoothHidden = false
  SmoothVisible = true
  Source = -> [Fusion005]
  Type = 2
  X = -51.338
  XDirection = (-0.582129,0.433096,0.688152)
  Y = 0
FEATURE [TechDraw::DrawProjGroupItem] ProjItem010  label="Bottom001"
  CoarseView = false
  Direction = (-0.813005,-0.322765,-0.48461)
  Focus = 100
  HardHidden = false
  IsoCount = 0
  IsoHidden = false
  IsoVisible = false
  LockPosition = false
  Perspective = false
  Rotation = 0
  RotationVector = (1,0,0)
  Scale = 1.5
  ScaleType = 2
  ScrubCount = 0
  SeamHidden = false
  SeamVisible = true
  SmoothHidden = false
  SmoothVisible = true
  Source = -> [Fusion005]
  Type = 5
  X = 0
  XDirection = (-0.012229,0.841576,-0.54)
  Y = 48.7411
FEATURE [TechDraw::DrawProjGroup] ProjGroup001
  Anchor = -> ProjItem005
  AutoDistribute = true
  LockPosition = false
  ProjectionType = 0
  Rotation = 0
  Scale = 1.5
  ScaleType = 2
  Source = -> [Fusion005]
  Views = -> [ProjItem005,ProjItem006,ProjItem007,ProjItem008,ProjItem009,ProjItem010]
  X = 148.5
  Y = 105
  spacingX = 0
  spacingY = 0
FEATURE [TechDraw::DrawPage] Page001
  KeepUpdated = true
  NextBalloonIndex = 1
  ProjectionType = 0
  Template = -> Template001
  Views = -> [ProjGroup001]
PROVENANCE & LICENSES
A FreeCAD (.FCStd) document from a public repository crawl; recipes are the document's own serialized feature recipes (and, for linked parts, companion documents' recipes).
License: bsd.
